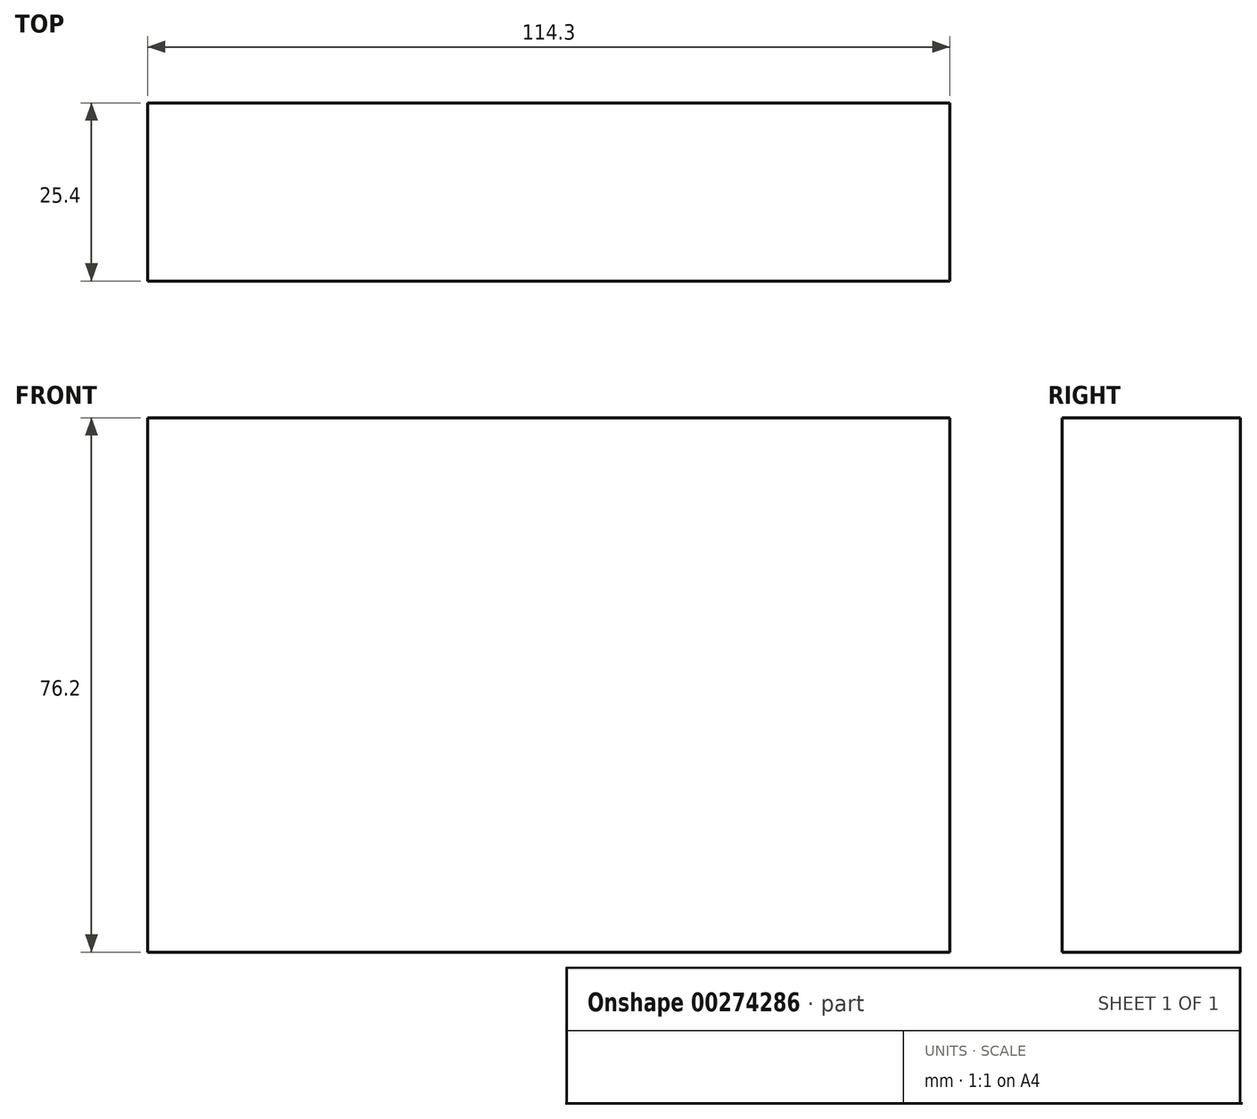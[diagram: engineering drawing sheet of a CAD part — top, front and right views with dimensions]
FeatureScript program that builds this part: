
annotation { "Feature Type Name" : "Feature", "Feature Type Description" : "" }
export const myFeature = defineFeature(function(context is Context, id is Id, definition is map)
    precondition{}
    {
        {
            var Q0;
            Q0=qCreatedBy(makeId("Front.planeOp"),FACE);
            var sketch = newSketch(context, id + "F0", { "sketchPlane" : qUnion([Q0])});
            skLineSegment(sketch, "E0.bottom", {"start": v(0, 0) * mm, "end": v(114.3, 0) * mm});
            skLineSegment(sketch, "E0.top", {"start": v(0, 76.2) * mm, "end": v(114.3, 76.2) * mm});
            skLineSegment(sketch, "E0.left", {"start": v(0, 0) * mm, "end": v(0, 76.2) * mm});
            skLineSegment(sketch, "E0.right", {"start": v(114.3, 0) * mm, "end": v(114.3, 76.2) * mm});
            skSolve(sketch);
        }
        {
            var Q0;
            Q0=makeQuery(id+"F0.imprint","IMPRINT",FACE,{"disambiguationData":[TD([[makeQuery(id+"F0.imprint","IMPRINT",EDGE,{"derivedFrom":sQuery(id+"F0.wireOp",EDGE,"E0.bottom")}),1.0]])]});
            extrude(context, id + "F1", {"entities" : qUnion([Q0]), "depth" : 25.4 * mm});
        }
    });
